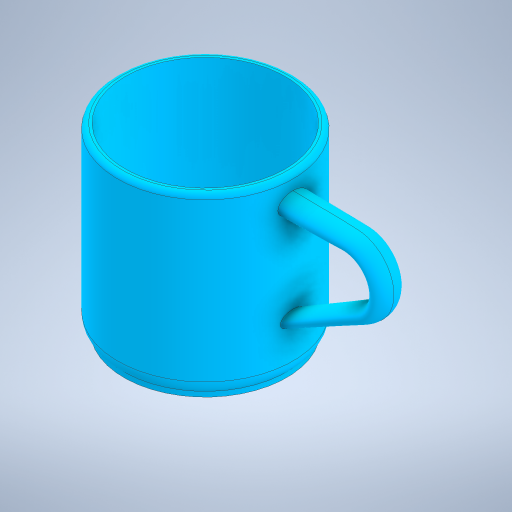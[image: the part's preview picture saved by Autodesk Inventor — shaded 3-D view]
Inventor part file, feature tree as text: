
AUTODESK INVENTOR PART (.ipt)
format: ipt  version: 2024 (Build 280153000, 153)  size: 373,760 bytes
history: native  units: mm
features: sketch x7, plane x2, other x1, revolve x1, shell x1, loft x1, fillet x1, extrude x1
ambient origin geometry x8: Origin, YZ Plane, XZ Plane, XY Plane, X Axis, Y Axis, Z Axis, Center Point
bodies: Solid1 (feature_tree)
feature tree (15):
  other  "CrossSection1"
  revolve  "Revolution1"  [1 undecoded]
  shell  "Shell1"  Thickness=65.0mm
  sketch  "Sketch2"  dims[d3=32.5mm d4=6.2mm d5=90.0deg]
  sketch  "Sketch3"  dims[d6=3.0mm d7=0.5mm d8=2.0mm d9=0.0mm d10=20.0mm]
  sketch  "Sketch4"  dims[d16=25.0mm]
  plane  "Work Plane1"
  sketch  "Sketch5"  dims[d17=12.0mm]
  plane  "Work Plane2"
  loft  "Loft1"
  fillet  "Fillet1"  [1 undecoded]
  extrude  "Extrusion1"  Depth=2.0mm TaperAngle=0.0deg
  sketch  "Sketch1"  dims[d0=70.0mm d1=35.0mm d2=65.0mm]
  sketch  "Sketch6"  dims[d18=4.0mm]
  sketch  "Sketch7"  dims[d19=6.0mm d20=3.0mm d21=5.0mm d22=0.0mm d23=90.0deg d24=0.0mm d25=90.0deg d26=0.0mm d27=90.0deg d28=2.0mm d29=65.0mm d30=62.0mm d31=2.0mm d32=0.0mm d33=0.5mm d34=0.872665mm]
note: 2 required parameter values undecoded (feature->parameter linkage not recoverable at this tier; creation-order binding heuristic only, values carry confidence <= 0.55)